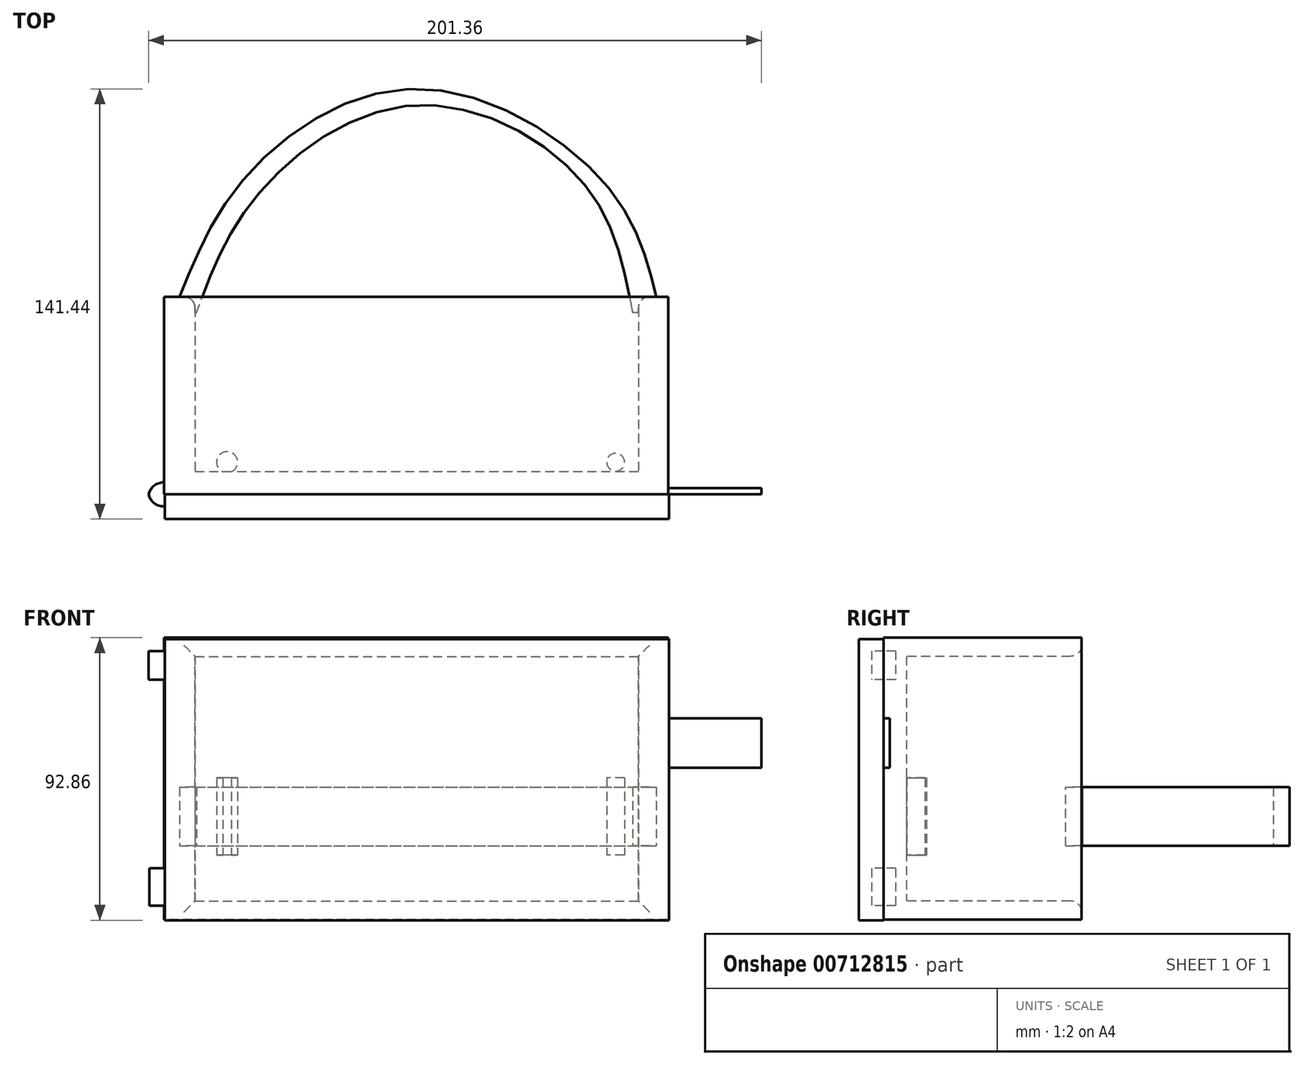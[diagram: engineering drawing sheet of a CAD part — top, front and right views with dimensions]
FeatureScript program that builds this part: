
annotation { "Feature Type Name" : "Feature", "Feature Type Description" : "" }
export const myFeature = defineFeature(function(context is Context, id is Id, definition is map)
    precondition{}
    {
        {
            var Q0;
            Q0=qCreatedBy(makeId("Front.planeOp"),FACE);
            var sketch = newSketch(context, id + "F0", { "sketchPlane" : qUnion([Q0])});
            skLineSegment(sketch, "E0.bottom", {"start": v(-82.55, 58.26) * mm, "end": v(83.06, 58.26) * mm});
            skLineSegment(sketch, "E0.top", {"start": v(-82.55, -34.1) * mm, "end": v(83.06, -34.1) * mm});
            skLineSegment(sketch, "E0.left", {"start": v(-82.55, 58.26) * mm, "end": v(-82.55, -34.1) * mm});
            skLineSegment(sketch, "E0.right", {"start": v(83.06, 58.26) * mm, "end": v(83.06, -34.1) * mm});
            skSolve(sketch);
        }
        {
            var Q0;
            Q0=makeQuery(id+"F0.imprint","IMPRINT",FACE,{"disambiguationData":[TD([[makeQuery(id+"F0.imprint","IMPRINT",EDGE,{"derivedFrom":sQuery(id+"F0.wireOp",EDGE,"E0.bottom")}),-1.0]])]});
            extrude(context, id + "F1", {"entities" : qUnion([Q0]), "depth" : 8.13 * mm, "offsetDistance" : 25.4 * mm});
        }
        {
            var Q0;
            Q0=qCreatedBy(makeId("Right.planeOp"),FACE);
            var sketch = newSketch(context, id + "F2", { "sketchPlane" : qUnion([Q0])});
            skLineSegment(sketch, "E1.bottom", {"start": v(0, 58.77) * mm, "end": v(65, 58.77) * mm});
            skLineSegment(sketch, "E1.top", {"start": v(0, 0) * mm, "end": v(65, 0) * mm});
            skLineSegment(sketch, "E1.left", {"start": v(0, 58.77) * mm, "end": v(0, 0) * mm});
            skLineSegment(sketch, "E1.right", {"start": v(65, 58.77) * mm, "end": v(65, 0) * mm});
            skLineSegment(sketch, "E2.bottom", {"start": v(65, 0) * mm, "end": v(0, 0) * mm});
            skLineSegment(sketch, "E2.top", {"start": v(65, -33.84) * mm, "end": v(0, -33.84) * mm});
            skLineSegment(sketch, "E2.left", {"start": v(65, 0) * mm, "end": v(65, -33.84) * mm});
            skLineSegment(sketch, "E2.right", {"start": v(0, 0) * mm, "end": v(0, -33.84) * mm});
            skSolve(sketch);
        }
        {
            var Q0;
            Q0 = qSketchRegion(id + "F2", true);
            extrude(context, id + "F3", {"entities" : qUnion([Q0]), "operationType" : NewBodyOperationType.ADD, "endBound" : BoundingType.SYMMETRIC, "depth" : 165.6 * mm, "offsetDistance" : 25.4 * mm});
        }
        {
            var Q0;
            Q0=qCreatedBy(makeId("Front.planeOp"),FACE);
            var sketch = newSketch(context, id + "F4", { "sketchPlane" : qUnion([Q0])});
            skLineSegment(sketch, "E3.bottom", {"start": v(73.02, 52.66) * mm, "end": v(-72.63, 52.66) * mm});
            skLineSegment(sketch, "E3.top", {"start": v(73.02, -27.73) * mm, "end": v(-72.63, -27.73) * mm});
            skLineSegment(sketch, "E3.left", {"start": v(73.02, 52.66) * mm, "end": v(73.02, -27.73) * mm});
            skLineSegment(sketch, "E3.right", {"start": v(-72.63, 52.66) * mm, "end": v(-72.63, -27.73) * mm});
            skSolve(sketch);
        }
        {
            var Q0;
            Q0 = qSketchRegion(id + "F4", true);
            extrude(context, id + "F5", {"entities" : qUnion([Q0]), "operationType" : NewBodyOperationType.REMOVE, "oppositeDirection" : true, "depth" : 126.5 * mm, "offsetDistance" : 25.4 * mm});
        }
        {
            var Q0;
            Q0=qCreatedBy(makeId("Top.planeOp"),FACE);
            var sketch = newSketch(context, id + "F6", { "sketchPlane" : qUnion([Q0])});
            skFitSpline(sketch, "E4", {"points": [v(-79.97, 59.74) * mm, v(-59.02, 100.67) * mm, v(0, 133.31) * mm, v(63.27, 100.67) * mm, v(78.86, 65.1) * mm], "startDerivative": vector(68.45, 154.85) * mm, "endDerivative": vector(40.9, -165.23) * mm});
            skLineSegment(sketch, "E5", {"start": v(-79.97, 59.74) * mm, "end": v(-72.18, 59.74) * mm});
            skLineSegment(sketch, "E6", {"start": v(78.86, 65.1) * mm, "end": v(78.86, 59.74) * mm});
            skLineSegment(sketch, "E7", {"start": v(78.86, 59.74) * mm, "end": v(71.07, 59.74) * mm});
            skLineSegment(sketch, "E8", {"start": v(71.07, 59.74) * mm, "end": v(78.86, 59.74) * mm});
            skFitSpline(sketch, "E9", {"points": [v(-72.18, 59.74) * mm, v(-52.69, 97.75) * mm, v(0, 127.95) * mm, v(55.48, 101.64) * mm, v(71.07, 59.74) * mm], "startDerivative": vector(62.26, 169.3) * mm, "endDerivative": vector(34.64, -188.72) * mm});
            skSolve(sketch);
        }
        {
            var Q0;
            Q0 = qSketchRegion(id + "F6", true);
            extrude(context, id + "F7", {"entities" : qUnion([Q0]), "operationType" : NewBodyOperationType.ADD, "endBound" : BoundingType.SYMMETRIC, "depth" : 19.3 * mm, "offsetDistance" : 25.4 * mm});
        }
        {
            var Q0;
            Q0=qCreatedBy(makeId("Right.planeOp"),FACE);
            var sketch = newSketch(context, id + "F8", { "sketchPlane" : qUnion([Q0])});
            skFitSpline(sketch, "E10", {"points": [v(49.54, 58.49) * mm, v(90.48, 61.9) * mm, v(129.67, 33.85) * mm, v(132.62, 9.47) * mm], "startDerivative": vector(110.05, 74.02) * mm, "endDerivative": vector(5.52, 30.5) * mm});
            skSolve(sketch);
        }
        {
            var Q0;
            Q0=sQuery(id+"F8.wireOp",EDGE,"E10");
            extrude(context, id + "F9", {"bodyType" : ToolBodyType.SURFACE, "surfaceEntities" : qUnion([Q0]), "endBound" : BoundingType.SYMMETRIC, "depth" : 25.4 * mm, "offsetDistance" : 25.4 * mm});
        }
        {
            var Q0;
            Q0=makeQuery(id+"F5.boolean.opBoolean","COPY",FACE,{"derivedFrom":makeQuery(id+"F5.opExtrude","CAP_FACE",FACE,{"disambiguationData":[OSD([sQuery(id+"F4.wireOp",EDGE,"E3.bottom"),sQuery(id+"F4.wireOp",EDGE,"E3.top"),sQuery(id+"F4.wireOp",EDGE,"E3.left"),sQuery(id+"F4.wireOp",EDGE,"E3.right")])],"isStart":true})});
            extrude(context, id + "F10", {"entities" : qUnion([Q0]), "operationType" : NewBodyOperationType.ADD, "depth" : 7.4 * mm, "offsetDistance" : 25.4 * mm});
        }
        {
            var Q0;
            Q0=makeQuery(id+"F5.boolean.opBoolean","INTERSECT",EDGE,{"derivedFrom":[makeQuery(id+"F3.opExtrude","SWEPT_FACE",FACE,{"disambiguationData":[OSD([sQuery(id+"F2.wireOp",EDGE,"E1.right"),sQuery(id+"F2.wireOp",EDGE,"E2.left")])]}),makeQuery(id+"F5.opExtrude","SWEPT_FACE",FACE,{"disambiguationData":[OSD([sQuery(id+"F4.wireOp",EDGE,"E3.top")])]})]});
            var Q1;
            Q1=makeQuery(id+"F5.boolean.opBoolean","INTERSECT",EDGE,{"derivedFrom":[makeQuery(id+"F3.opExtrude","SWEPT_FACE",FACE,{"disambiguationData":[OSD([sQuery(id+"F2.wireOp",EDGE,"E1.right"),sQuery(id+"F2.wireOp",EDGE,"E2.left")])]}),makeQuery(id+"F5.opExtrude","SWEPT_FACE",FACE,{"disambiguationData":[OSD([sQuery(id+"F4.wireOp",EDGE,"E3.bottom")])]})]});
            var Q2;
            {var subQ0=makeQuery(id+"F3.opExtrude","SWEPT_FACE",FACE,{"disambiguationData":[OSD([sQuery(id+"F2.wireOp",EDGE,"E1.right"),sQuery(id+"F2.wireOp",EDGE,"E2.left")])]});var subQ1=makeQuery(id+"F5.opExtrude","SWEPT_FACE",FACE,{"disambiguationData":[OSD([sQuery(id+"F4.wireOp",EDGE,"E3.right")])]});Q2=makeQuery(id+"F7.boolean.opBoolean","SPLIT",EDGE,{"disambiguationData":[TD([makeQuery(id+"F5.boolean.opBoolean","COPY",FACE,{"derivedFrom":makeQuery(id+"F5.opExtrude","SWEPT_FACE",FACE,{"disambiguationData":[OSD([sQuery(id+"F4.wireOp",EDGE,"E3.bottom")])]})})])],"derivedFrom":makeQuery(id+"F5.boolean.opBoolean","INTERSECT",EDGE,{"derivedFrom":[subQ0,subQ1]})});}
            var Q3;
            {var subQ0=makeQuery(id+"F3.opExtrude","SWEPT_FACE",FACE,{"disambiguationData":[OSD([sQuery(id+"F2.wireOp",EDGE,"E1.right"),sQuery(id+"F2.wireOp",EDGE,"E2.left")])]});var subQ1=makeQuery(id+"F5.opExtrude","SWEPT_FACE",FACE,{"disambiguationData":[OSD([sQuery(id+"F4.wireOp",EDGE,"E3.left")])]});Q3=makeQuery(id+"F7.boolean.opBoolean","SPLIT",EDGE,{"disambiguationData":[TD([makeQuery(id+"F5.boolean.opBoolean","COPY",FACE,{"derivedFrom":makeQuery(id+"F5.opExtrude","SWEPT_FACE",FACE,{"disambiguationData":[OSD([sQuery(id+"F4.wireOp",EDGE,"E3.bottom")])]})})])],"derivedFrom":makeQuery(id+"F5.boolean.opBoolean","INTERSECT",EDGE,{"derivedFrom":[subQ0,subQ1]})});}
            var Q4;
            {var subQ0=makeQuery(id+"F3.opExtrude","SWEPT_FACE",FACE,{"disambiguationData":[OSD([sQuery(id+"F2.wireOp",EDGE,"E1.right"),sQuery(id+"F2.wireOp",EDGE,"E2.left")])]});var subQ1=makeQuery(id+"F5.opExtrude","SWEPT_FACE",FACE,{"disambiguationData":[OSD([sQuery(id+"F4.wireOp",EDGE,"E3.left")])]});Q4=makeQuery(id+"F7.boolean.opBoolean","SPLIT",EDGE,{"disambiguationData":[TD([makeQuery(id+"F5.boolean.opBoolean","COPY",FACE,{"derivedFrom":makeQuery(id+"F5.opExtrude","SWEPT_FACE",FACE,{"disambiguationData":[OSD([sQuery(id+"F4.wireOp",EDGE,"E3.top")])]})})])],"derivedFrom":makeQuery(id+"F5.boolean.opBoolean","INTERSECT",EDGE,{"derivedFrom":[subQ0,subQ1]})});}
            var Q5;
            {var subQ0=makeQuery(id+"F3.opExtrude","SWEPT_FACE",FACE,{"disambiguationData":[OSD([sQuery(id+"F2.wireOp",EDGE,"E1.right"),sQuery(id+"F2.wireOp",EDGE,"E2.left")])]});var subQ1=makeQuery(id+"F5.opExtrude","SWEPT_FACE",FACE,{"disambiguationData":[OSD([sQuery(id+"F4.wireOp",EDGE,"E3.right")])]});Q5=makeQuery(id+"F7.boolean.opBoolean","SPLIT",EDGE,{"disambiguationData":[TD([makeQuery(id+"F5.boolean.opBoolean","COPY",FACE,{"derivedFrom":makeQuery(id+"F5.opExtrude","SWEPT_FACE",FACE,{"disambiguationData":[OSD([sQuery(id+"F4.wireOp",EDGE,"E3.top")])]})})])],"derivedFrom":makeQuery(id+"F5.boolean.opBoolean","INTERSECT",EDGE,{"derivedFrom":[subQ0,subQ1]})});}
            fillet(context, id + "F11", {"entities" : qUnion([Q0, Q1, Q2, Q3, Q4, Q5]), "radius" : 3.68 * mm, "tangentPropagation" : true, "allowEdgeOverflow" : false});
        }
        {
            var Q0;
            Q0=qCreatedBy(makeId("Front.planeOp"),FACE);
            var sketch = newSketch(context, id + "F12", { "sketchPlane" : qUnion([Q0])});
            skLineSegment(sketch, "E11.bottom", {"start": v(-88.02, 54.44) * mm, "end": v(-77.08, 54.44) * mm});
            skLineSegment(sketch, "E11.top", {"start": v(-88.02, 45.03) * mm, "end": v(-77.08, 45.03) * mm});
            skLineSegment(sketch, "E11.left", {"start": v(-88.02, 54.44) * mm, "end": v(-88.02, 45.03) * mm});
            skLineSegment(sketch, "E11.right", {"start": v(-77.08, 54.44) * mm, "end": v(-77.08, 45.03) * mm});
            skLineSegment(sketch, "E12.bottom", {"start": v(-87.77, -17.05) * mm, "end": v(-78.86, -17.05) * mm});
            skLineSegment(sketch, "E12.top", {"start": v(-87.77, -29.26) * mm, "end": v(-78.86, -29.26) * mm});
            skLineSegment(sketch, "E12.left", {"start": v(-87.77, -17.05) * mm, "end": v(-87.77, -29.26) * mm});
            skLineSegment(sketch, "E12.right", {"start": v(-78.86, -17.05) * mm, "end": v(-78.86, -29.26) * mm});
            skSolve(sketch);
        }
        {
            var Q0;
            Q0 = qSketchRegion(id + "F12", true);
            extrude(context, id + "F13", {"entities" : qUnion([Q0]), "operationType" : NewBodyOperationType.ADD, "endBound" : BoundingType.SYMMETRIC, "depth" : 7.87 * mm, "offsetDistance" : 25.4 * mm});
        }
        {
            var Q0;
            Q0=makeQuery(id+"F13.opExtrude","CAP_EDGE",EDGE,{"disambiguationData":[OSD([sQuery(id+"F12.wireOp",EDGE,"E11.left")])],"isStart":true});
            var Q1;
            Q1=makeQuery(id+"F13.opExtrude","CAP_EDGE",EDGE,{"disambiguationData":[OSD([sQuery(id+"F12.wireOp",EDGE,"E11.left")])],"isStart":false});
            var Q2;
            Q2=makeQuery(id+"F13.opExtrude","CAP_EDGE",EDGE,{"disambiguationData":[OSD([sQuery(id+"F12.wireOp",EDGE,"E12.left")])],"isStart":true});
            var Q3;
            Q3=makeQuery(id+"F13.opExtrude","CAP_EDGE",EDGE,{"disambiguationData":[OSD([sQuery(id+"F12.wireOp",EDGE,"E12.left")])],"isStart":false});
            fillet(context, id + "F14", {"entities" : qUnion([Q0, Q1, Q2, Q3]), "radius" : 5.08 * mm, "tangentPropagation" : true, "allowEdgeOverflow" : false});
        }
        {
            var Q0;
            Q0=qCreatedBy(makeId("Top.planeOp"),FACE);
            var sketch = newSketch(context, id + "F15", { "sketchPlane" : qUnion([Q0])});
            skLineSegment(sketch, "E13", {"start": v(-74.5, 42.2) * mm, "end": v(-62.08, 9.82) * mm});
            skLineSegment(sketch, "E14", {"start": v(72.3, 42.2) * mm, "end": v(65.53, 9.82) * mm});
            skSolve(sketch);
        }
        {
            var Q0;
            Q0=sQuery(id+"F15.wireOp",EDGE,"E14");
            var Q1;
            Q1=sQuery(id+"F15.wireOp",EDGE,"E13");
            extrude(context, id + "F16", {"bodyType" : ToolBodyType.SURFACE, "surfaceEntities" : qUnion([Q0, Q1]), "endBound" : BoundingType.SYMMETRIC, "depth" : 25.4 * mm, "offsetDistance" : 25.4 * mm});
        }
        {
            var Q0;
            Q0=qCreatedBy(makeId("Top.planeOp"),FACE);
            var sketch = newSketch(context, id + "F17", { "sketchPlane" : qUnion([Q0])});
            skCircle(sketch, "E15", {"center": v(-62.08, 10.57) * mm, "radius": 3.47 * mm});
            skCircle(sketch, "E16", {"center": v(65.53, 10.57) * mm, "radius": 2.94 * mm});
            skSolve(sketch);
        }
        {
            var Q0;
            Q0 = qSketchRegion(id + "F17", true);
            extrude(context, id + "F18", {"entities" : qUnion([Q0]), "operationType" : NewBodyOperationType.ADD, "endBound" : BoundingType.SYMMETRIC, "depth" : 25.4 * mm, "offsetDistance" : 25.4 * mm});
        }
        {
            var Q0;
            Q0=qCreatedBy(makeId("Front.planeOp"),FACE);
            var sketch = newSketch(context, id + "F19", { "sketchPlane" : qUnion([Q0])});
            skLineSegment(sketch, "E17.bottom", {"start": v(79.12, 32.3) * mm, "end": v(113.47, 32.3) * mm});
            skLineSegment(sketch, "E17.top", {"start": v(79.12, 16.03) * mm, "end": v(113.47, 16.03) * mm});
            skLineSegment(sketch, "E17.left", {"start": v(79.12, 32.3) * mm, "end": v(79.12, 16.03) * mm});
            skLineSegment(sketch, "E17.right", {"start": v(113.47, 32.3) * mm, "end": v(113.47, 16.03) * mm});
            skSolve(sketch);
        }
        {
            var Q0;
            Q0 = qSketchRegion(id + "F19", true);
            extrude(context, id + "F20", {"entities" : qUnion([Q0]), "operationType" : NewBodyOperationType.ADD, "oppositeDirection" : true, "depth" : 2.03 * mm, "offsetDistance" : 25.4 * mm});
        }
    });
